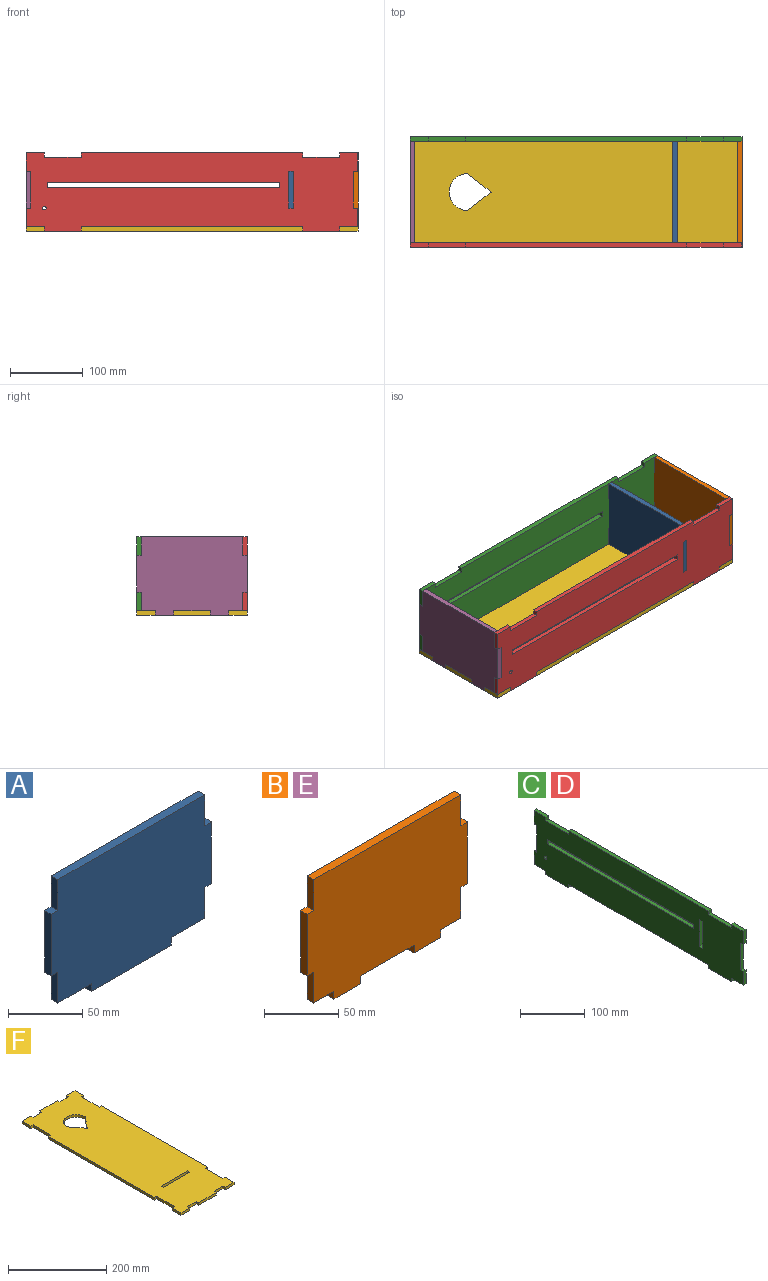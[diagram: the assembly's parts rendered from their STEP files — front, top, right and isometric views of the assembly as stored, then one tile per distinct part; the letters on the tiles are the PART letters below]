
ASSEMBLY  parts=6 mates=5
PART A: 18 faces, bbox 152.4x6.4x108 mm
  f0: plane 25.4x6.35mm, normal (1,0,0), area 161.3mm2, adj f2,f7,f8,f15
  f1: plane 25.4x6.35mm, normal (-1,0,0), area 161.3mm2, adj f4,f7,f8,f12
  f2: plane 31.75x6.35mm, normal (0,0,-1), area 201.6mm2, adj f0,f7,f8,f9
  f3: plane 25.4x6.35mm, normal (-1,0,0), area 161.3mm2, adj f6,f7,f8,f13
  f4: plane 31.75x6.35mm, normal (0,0,-1), area 201.6mm2, adj f1,f7,f8,f10
  f5: plane 25.4x6.35mm, normal (1,0,0), area 161.3mm2, adj f6,f7,f8,f17
  f6: plane 139.7x6.35mm, normal (0,0,1), area 887.1mm2, adj f3,f5,f7,f8
  f7: plane 152.4x107.95mm, normal (0,-1,0), area 15322.6mm2, adj f0,f1,f2,f3,f4,f5,f6,f9
  f8: plane 152.4x107.95mm, normal (0,1,0), area 15322.6mm2, adj f0,f1,f2,f3,f4,f5,f6,f9
  f9: plane 6.35x6.35mm, normal (1,0,0), area 40.3mm2, adj f2,f7,f8,f11
  f10: plane 6.35x6.35mm, normal (-1,0,0), area 40.3mm2, adj f4,f7,f8,f11
  f11: plane 76.2x6.35mm, normal (0,0,-1), area 483.9mm2, adj f7,f8,f9,f10
  f12: plane 6.35x6.35mm, normal (0,0,-1), area 40.3mm2, adj f1,f7,f8,f14
  f13: plane 6.35x6.35mm, normal (0,0,1), area 40.3mm2, adj f3,f7,f8,f14
  f14: plane 50.8x6.35mm, normal (-1,0,0), area 322.6mm2, adj f7,f8,f12,f13
  f15: plane 6.35x6.35mm, normal (0,0,-1), area 40.3mm2, adj f0,f7,f8,f16
  f16: plane 50.8x6.35mm, normal (1,0,0), area 322.6mm2, adj f7,f8,f15,f17
  f17: plane 6.35x6.35mm, normal (0,0,1), area 40.3mm2, adj f5,f7,f8,f16
PART B: 22 faces, bbox 152.4x6.4x108 mm
  f0: plane 25.4x6.35mm, normal (0,0,-1), area 161.3mm2, adj f1,f2,f3,f4
  f1: plane 6.35x6.35mm, normal (1,0,0), area 40.3mm2, adj f0,f3,f4,f8
  f2: plane 6.35x6.35mm, normal (-1,0,0), area 40.3mm2, adj f0,f3,f4,f5
  f3: plane 152.4x107.95mm, normal (0,1,0), area 15161.3mm2, adj f0,f1,f2,f5,f6,f7,f8,f9
  f4: plane 152.4x107.95mm, normal (0,-1,0), area 15161.3mm2, adj f0,f1,f2,f5,f6,f7,f8,f9
  f5: plane 19.05x6.35mm, normal (0,0,-1), area 121mm2, adj f2,f3,f4,f16
  f6: plane 19.05x6.35mm, normal (0,0,-1), area 121mm2, adj f3,f4,f13,f21
  f7: plane 50.8x6.35mm, normal (-1,0,0), area 322.6mm2, adj f3,f4,f15,f18
  f8: plane 50.8x6.35mm, normal (0,0,-1), area 322.6mm2, adj f1,f3,f4,f19
  f9: plane 50.8x6.35mm, normal (1,0,0), area 322.6mm2, adj f3,f4,f12,f14
  f10: plane 139.7x6.35mm, normal (0,0,1), area 887.1mm2, adj f3,f4,f11,f17
  f11: plane 25.4x6.35mm, normal (1,0,0), area 161.3mm2, adj f3,f4,f10,f12
  f12: plane 6.35x6.35mm, normal (0,0,1), area 40.3mm2, adj f3,f4,f9,f11
  f13: plane 25.4x6.35mm, normal (1,0,0), area 161.3mm2, adj f3,f4,f6,f14
  f14: plane 6.35x6.35mm, normal (0,0,-1), area 40.3mm2, adj f3,f4,f9,f13
  f15: plane 6.35x6.35mm, normal (0,0,-1), area 40.3mm2, adj f3,f4,f7,f16
  f16: plane 25.4x6.35mm, normal (-1,0,0), area 161.3mm2, adj f3,f4,f5,f15
  f17: plane 25.4x6.35mm, normal (-1,0,0), area 161.3mm2, adj f3,f4,f10,f18
  f18: plane 6.35x6.35mm, normal (0,0,1), area 40.3mm2, adj f3,f4,f7,f17
  f19: plane 6.35x6.35mm, normal (-1,0,0), area 40.3mm2, adj f3,f4,f8,f20
  f20: plane 25.4x6.35mm, normal (0,0,-1), area 161.3mm2, adj f3,f4,f19,f21
  f21: plane 6.35x6.35mm, normal (1,0,0), area 40.3mm2, adj f3,f4,f6,f20
PART C: 39 faces, bbox 6.4x457.2x108 mm
  f0: plane 304.8x6.35mm, normal (0,0,1), area 1935.5mm2, adj f2,f3,f30,f32
  f1: plane 25.4x6.35mm, normal (0,0,1), area 161.3mm2, adj f2,f3,f13,f29
  f2: plane 457.2x107.95mm, normal (-1,0,0), area 43024.8mm2, adj f0,f1,f4,f5,f6,f7,f8,f9
  f3: plane 457.2x107.95mm, normal (1,0,0), area 43024.8mm2, adj f0,f1,f4,f5,f6,f7,f8,f9
  f4: plane 6.35x6.35mm, normal (0,-1,0), area 40.3mm2, adj f2,f3,f5,f7
  f5: plane 50.8x6.35mm, normal (0,0,-1), area 322.6mm2, adj f2,f3,f4,f6
  f6: plane 6.35x6.35mm, normal (0,1,0), area 40.3mm2, adj f2,f3,f5,f12
  f7: plane 25.4x6.35mm, normal (0,0,-1), area 161.3mm2, adj f2,f3,f4,f9
  f8: plane 25.4x6.35mm, normal (0,0,-1), area 161.3mm2, adj f2,f3,f10,f24
  f9: plane 25.4x6.35mm, normal (0,-1,0), area 161.3mm2, adj f2,f3,f7,f16
  f10: plane 25.4x6.35mm, normal (0,1,0), area 161.3mm2, adj f2,f3,f8,f19
  f11: plane 25.4x6.35mm, normal (0,-1,0), area 161.3mm2, adj f2,f3,f14,f18
  f12: plane 304.8x6.35mm, normal (0,0,-1), area 1935.5mm2, adj f2,f3,f6,f22
  f13: plane 25.4x6.35mm, normal (0,1,0), area 161.3mm2, adj f1,f2,f3,f20
  f14: plane 25.4x6.35mm, normal (0,0,1), area 161.3mm2, adj f2,f3,f11,f33
  f15: cylinder r=2.54mm len=6.35mm, axis (1,0,0), area 101.3mm2, adj f2,f3
  f16: plane 6.35x6.35mm, normal (0,0,1), area 40.3mm2, adj f2,f3,f9,f17
  f17: plane 50.8x6.35mm, normal (0,-1,0), area 322.6mm2, adj f2,f3,f16,f18
  f18: plane 6.35x6.35mm, normal (0,0,-1), area 40.3mm2, adj f2,f3,f11,f17
  f19: plane 6.35x6.35mm, normal (0,0,1), area 40.3mm2, adj f2,f3,f10,f21
  f20: plane 6.35x6.35mm, normal (0,0,-1), area 40.3mm2, adj f2,f3,f13,f21
  f21: plane 50.8x6.35mm, normal (0,1,0), area 322.6mm2, adj f2,f3,f19,f20
  f22: plane 6.35x6.35mm, normal (0,-1,0), area 40.3mm2, adj f2,f3,f12,f23
  f23: plane 50.8x6.35mm, normal (0,0,-1), area 322.6mm2, adj f2,f3,f22,f24
  f24: plane 6.35x6.35mm, normal (0,1,0), area 40.3mm2, adj f2,f3,f8,f23
  f25: plane 50.8x6.35mm, normal (0,1,0), area 322.6mm2, adj f2,f3,f26,f28
  f26: plane 6.35x6.35mm, normal (0,0,1), area 40.3mm2, adj f2,f3,f25,f27
  f27: plane 50.8x6.35mm, normal (0,-1,0), area 322.6mm2, adj f2,f3,f26,f28
  f28: plane 6.35x6.35mm, normal (0,0,-1), area 40.3mm2, adj f2,f3,f25,f27
  f29: plane 6.35x6.35mm, normal (0,-1,0), area 40.3mm2, adj f1,f2,f3,f31
  f30: plane 6.35x6.35mm, normal (0,1,0), area 40.3mm2, adj f0,f2,f3,f31
  f31: plane 50.8x6.35mm, normal (0,0,1), area 322.6mm2, adj f2,f3,f29,f30
  f32: plane 6.35x6.35mm, normal (0,-1,0), area 40.3mm2, adj f0,f2,f3,f34
  f33: plane 6.35x6.35mm, normal (0,1,0), area 40.3mm2, adj f2,f3,f14,f34
  f34: plane 50.8x6.35mm, normal (0,0,1), area 322.6mm2, adj f2,f3,f32,f33
  f35: plane 7.62x6.35mm, normal (0,1,0), area 48.4mm2, adj f2,f3,f36,f38
  f36: plane 320.04x6.35mm, normal (0,0,1), area 2032.3mm2, adj f2,f3,f35,f37
  f37: plane 7.62x6.35mm, normal (0,-1,0), area 48.4mm2, adj f2,f3,f36,f38
  f38: plane 320.04x6.35mm, normal (0,0,-1), area 2032.3mm2, adj f2,f3,f35,f37
PART D: same geometry as C
PART E: same geometry as B
PART F: 45 faces, bbox 152.4x457.2x6.4 mm
  f0: plane 457.2x152.4mm, normal (0,0,1), area 65418.4mm2, adj f2,f3,f4,f5,f6,f7,f8,f9
  f1: plane 457.2x152.4mm, normal (0,0,-1), area 65418.4mm2, adj f2,f3,f4,f5,f6,f7,f8,f9
  f2: plane 304.8x6.35mm, normal (-1,0,0), area 1935.5mm2, adj f0,f1,f34,f35
  f3: plane 25.4x6.35mm, normal (-1,0,0), area 161.3mm2, adj f0,f1,f11,f32
  f4: plane 304.8x6.35mm, normal (1,0,0), area 1935.5mm2, adj f0,f1,f27,f29
  f5: plane 25.4x6.35mm, normal (1,0,0), area 161.3mm2, adj f0,f1,f6,f26
  f6: plane 25.4x6.35mm, normal (0,-1,0), area 161.3mm2, adj f0,f1,f5,f24
  f7: plane 50.8x6.35mm, normal (0,-1,0), area 322.6mm2, adj f0,f1,f20,f23
  f8: plane 25.4x6.35mm, normal (0,1,0), area 161.3mm2, adj f0,f1,f12,f19
  f9: plane 50.8x6.35mm, normal (0,1,0), area 322.6mm2, adj f0,f1,f14,f17
  f10: plane 25.4x6.35mm, normal (-1,0,0), area 161.3mm2, adj f0,f1,f13,f37
  f11: plane 25.4x6.35mm, normal (0,-1,0), area 161.3mm2, adj f0,f1,f3,f22
  f12: plane 25.4x6.35mm, normal (1,0,0), area 161.3mm2, adj f0,f1,f8,f30
  f13: plane 25.4x6.35mm, normal (0,1,0), area 161.3mm2, adj f0,f1,f10,f15
  f14: plane 6.35x6.35mm, normal (-1,0,0), area 40.3mm2, adj f0,f1,f9,f16
  f15: plane 6.35x6.35mm, normal (1,0,0), area 40.3mm2, adj f0,f1,f13,f16
  f16: plane 25.4x6.35mm, normal (0,1,0), area 161.3mm2, adj f0,f1,f14,f15
  f17: plane 6.35x6.35mm, normal (1,0,0), area 40.3mm2, adj f0,f1,f9,f18
  f18: plane 25.4x6.35mm, normal (0,1,0), area 161.3mm2, adj f0,f1,f17,f19
  f19: plane 6.35x6.35mm, normal (-1,0,0), area 40.3mm2, adj f0,f1,f8,f18
  f20: plane 6.35x6.35mm, normal (-1,0,0), area 40.3mm2, adj f0,f1,f7,f21
  f21: plane 25.4x6.35mm, normal (0,-1,0), area 161.3mm2, adj f0,f1,f20,f22
  f22: plane 6.35x6.35mm, normal (1,0,0), area 40.3mm2, adj f0,f1,f11,f21
  f23: plane 6.35x6.35mm, normal (1,0,0), area 40.3mm2, adj f0,f1,f7,f25
  f24: plane 6.35x6.35mm, normal (-1,0,0), area 40.3mm2, adj f0,f1,f6,f25
  f25: plane 25.4x6.35mm, normal (0,-1,0), area 161.3mm2, adj f0,f1,f23,f24
  f26: plane 6.35x6.35mm, normal (0,1,0), area 40.3mm2, adj f0,f1,f5,f28
  f27: plane 6.35x6.35mm, normal (0,-1,0), area 40.3mm2, adj f0,f1,f4,f28
  f28: plane 50.8x6.35mm, normal (1,0,0), area 322.6mm2, adj f0,f1,f26,f27
  f29: plane 6.35x6.35mm, normal (0,1,0), area 40.3mm2, adj f0,f1,f4,f31
  f30: plane 6.35x6.35mm, normal (0,-1,0), area 40.3mm2, adj f0,f1,f12,f31
  f31: plane 50.8x6.35mm, normal (1,0,0), area 322.6mm2, adj f0,f1,f29,f30
  f32: plane 6.35x6.35mm, normal (0,1,0), area 40.3mm2, adj f0,f1,f3,f33
  f33: plane 50.8x6.35mm, normal (-1,0,0), area 322.6mm2, adj f0,f1,f32,f34
  f34: plane 6.35x6.35mm, normal (0,-1,0), area 40.3mm2, adj f0,f1,f2,f33
  f35: plane 6.35x6.35mm, normal (0,1,0), area 40.3mm2, adj f0,f1,f2,f36
  f36: plane 50.8x6.35mm, normal (-1,0,0), area 322.6mm2, adj f0,f1,f35,f37
  f37: plane 6.35x6.35mm, normal (0,-1,0), area 40.3mm2, adj f0,f1,f10,f36
  f38: plane 6.35x6.35mm, normal (1,0,0), area 40.3mm2, adj f0,f1,f39,f41
  f39: plane 76.2x6.35mm, normal (0,1,0), area 483.9mm2, adj f0,f1,f38,f40
  f40: plane 6.35x6.35mm, normal (-1,0,0), area 40.3mm2, adj f0,f1,f39,f41
  f41: plane 76.2x6.35mm, normal (0,-1,0), area 483.9mm2, adj f0,f1,f38,f40
  f42: plane 31.9x25.4mm, normal (-0.78,0.62,0), area 258.9mm2, adj f0,f1,f43,f44
  f43: cylinder r=25.4mm len=50.8mm, axis (0,0,1), area 510.7mm2, adj f0,f1,f42,f44
  f44: plane 31.9x25.4mm, normal (0.78,0.62,0), area 258.9mm2, adj f0,f1,f42,f43
PLACE A rot(axis=(0,0,1),90deg) t=(304.05,47.16,-175.85)mm
PLACE B rot(axis=(0,0,1),90deg) t=(392.95,47.16,-175.85)mm
PLACE C rot(axis=(0,0,1),90deg) t=(170.7,117.01,-175.85)mm
PLACE D rot(axis=(0,0,1),90deg) t=(170.7,-29.04,-175.85)mm
PLACE E rot(axis=(0,0,-1),90deg) t=(-51.55,47.16,-175.85)mm
PLACE F rot(axis=(0,0,1),90deg) t=(170.7,47.16,-182.2)mm
MATE fastened B.f1 <-> F.f20  axis (0,1,0) through (396.13,21.76,-179.03)mm
MATE fastened E.f2 <-> F.f19  axis (0,1,0) through (-54.72,97.96,-179.03)mm
MATE fastened A.f9 <-> F.f40  axis (0,1,0) through (307.23,85.26,-179.03)mm
MATE fastened C.f4 <-> F.f26  axis (1,0,0) through (373.9,120.18,-179.03)mm
MATE fastened D.f22 <-> F.f35  axis (1,0,0) through (18.3,-25.87,-179.03)mm
